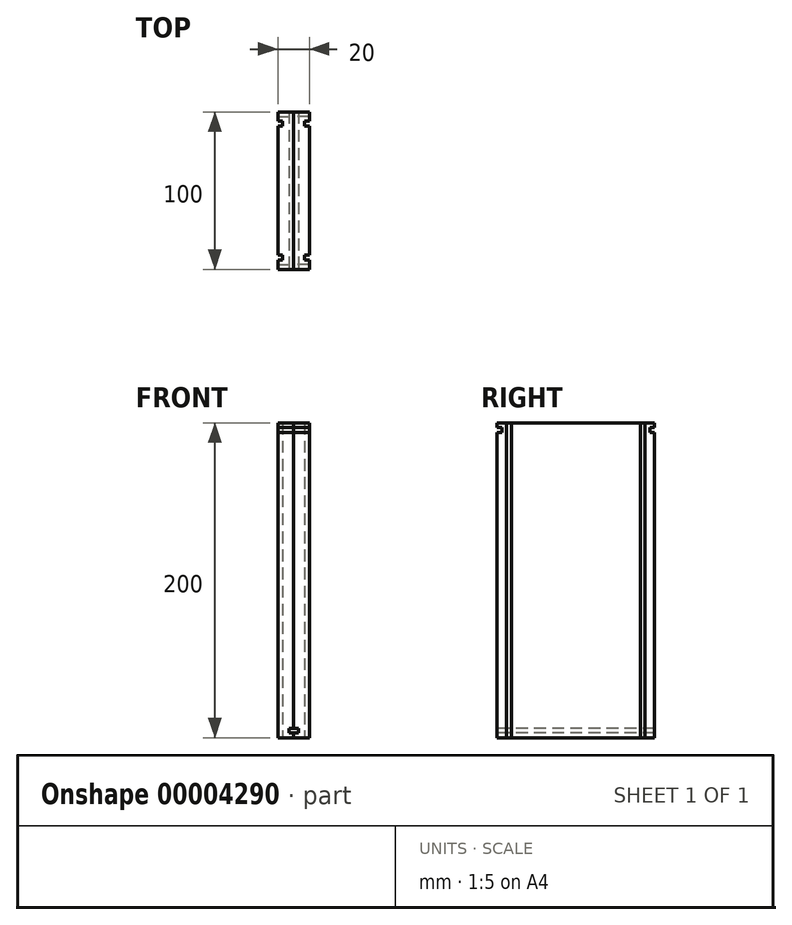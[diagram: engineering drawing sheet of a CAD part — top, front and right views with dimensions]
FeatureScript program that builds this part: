
annotation { "Feature Type Name" : "Feature", "Feature Type Description" : "" }
export const myFeature = defineFeature(function(context is Context, id is Id, definition is map)
    precondition{}
    {
        {
            var Q0;
            Q0=qCreatedBy(makeId("Right.planeOp"),FACE);
            var sketch = newSketch(context, id + "F0", { "sketchPlane" : qUnion([Q0])});
            skLineSegment(sketch, "E0", {"start": v(-61.66, 167.02) * mm, "end": v(38.34, 167.02) * mm});
            skLineSegment(sketch, "E1", {"start": v(38.34, 167.02) * mm, "end": v(38.34, -32.98) * mm});
            skLineSegment(sketch, "E2", {"start": v(38.34, -32.98) * mm, "end": v(-61.66, -32.98) * mm});
            skLineSegment(sketch, "E3", {"start": v(-61.66, -32.98) * mm, "end": v(-61.66, 167.02) * mm});
            skSolve(sketch);
        }
        {
            var Q0;
            Q0=makeQuery(id+"F0.imprint","IMPRINT",FACE,{"disambiguationData":[TD([[makeQuery(id+"F0.imprint","IMPRINT",EDGE,{"derivedFrom":sQuery(id+"F0.wireOp",EDGE,"E0")}),-1.0]])]});
            extrude(context, id + "F1", {"entities" : qUnion([Q0]), "depth" : 10 * mm});
        }
        {
            var Q0;
            Q0=makeQuery(id+"F1.opExtrude","CAP_FACE",FACE,{"disambiguationData":[OSD([sQuery(id+"F0.wireOp",EDGE,"E0"),sQuery(id+"F0.wireOp",EDGE,"E1"),sQuery(id+"F0.wireOp",EDGE,"E2"),sQuery(id+"F0.wireOp",EDGE,"E3")])],"isStart":true});
            var sketch = newSketch(context, id + "F2", { "sketchPlane" : qUnion([Q0])});
            skLineSegment(sketch, "E4.0", {"start": v(-38.34, -29.98) * mm, "end": v(61.66, -29.98) * mm});
            skLineSegment(sketch, "E5.0", {"start": v(-38.34, -26.98) * mm, "end": v(61.66, -26.98) * mm});
            skSolve(sketch);
        }
        {
            var Q0;
            {var subQ2=sQuery(id+"F2.wireOp",EDGE,"E4.0");Q0=makeQuery(id+"F2.imprint","IMPRINT",FACE,{"disambiguationData":[TD([[makeQuery(id+"F2.imprint","IMPRINT",EDGE,{"derivedFrom":subQ2}),1.0]])]});}
            extrude(context, id + "F3", {"entities" : qUnion([Q0]), "operationType" : NewBodyOperationType.REMOVE, "oppositeDirection" : true, "depth" : 3 * mm});
        }
        {
            var Q0;
            Q0=makeQuery(id+"F1.opExtrude","SWEPT_FACE",FACE,{"disambiguationData":[OSD([sQuery(id+"F0.wireOp",EDGE,"E1")])]});
            var sketch = newSketch(context, id + "F4", { "sketchPlane" : qUnion([Q0])});
            skLineSegment(sketch, "E6.0", {"start": v(-10, 164.02) * mm, "end": v(0, 164.02) * mm});
            skLineSegment(sketch, "E7.0", {"start": v(-10, 161.02) * mm, "end": v(0, 161.02) * mm});
            skSolve(sketch);
        }
        {
            var Q0;
            {var subQ4=sQuery(id+"F4.wireOp",EDGE,"E6.0");Q0=makeQuery(id+"F4.imprint","IMPRINT",FACE,{"disambiguationData":[TD([[makeQuery(id+"F4.imprint","IMPRINT",EDGE,{"derivedFrom":subQ4}),-1.0]])]});}
            extrude(context, id + "F5", {"entities" : qUnion([Q0]), "operationType" : NewBodyOperationType.REMOVE, "oppositeDirection" : true, "depth" : 3 * mm});
        }
        {
            var Q0;
            Q0=makeQuery(id+"F1.opExtrude","SWEPT_FACE",FACE,{"disambiguationData":[OSD([sQuery(id+"F0.wireOp",EDGE,"E3")])]});
            var sketch = newSketch(context, id + "F6", { "sketchPlane" : qUnion([Q0])});
            skLineSegment(sketch, "E8.0", {"start": v(10, 164.02) * mm, "end": v(0, 164.02) * mm});
            skLineSegment(sketch, "E9.0", {"start": v(10, 161.02) * mm, "end": v(0, 161.02) * mm});
            skSolve(sketch);
        }
        {
            var Q0;
            {var subQ4=sQuery(id+"F6.wireOp",EDGE,"E8.0");Q0=makeQuery(id+"F6.imprint","IMPRINT",FACE,{"disambiguationData":[TD([[makeQuery(id+"F6.imprint","IMPRINT",EDGE,{"derivedFrom":subQ4}),1.0]])]});}
            extrude(context, id + "F7", {"entities" : qUnion([Q0]), "operationType" : NewBodyOperationType.REMOVE, "oppositeDirection" : true, "depth" : 3 * mm});
        }
        {
            var Q0;
            Q0=makeQuery(id+"F1.opExtrude","CAP_FACE",FACE,{"disambiguationData":[OSD([sQuery(id+"F0.wireOp",EDGE,"E0"),sQuery(id+"F0.wireOp",EDGE,"E1"),sQuery(id+"F0.wireOp",EDGE,"E2"),sQuery(id+"F0.wireOp",EDGE,"E3")])],"isStart":false});
            var sketch = newSketch(context, id + "F8", { "sketchPlane" : qUnion([Q0])});
            skLineSegment(sketch, "E10.0", {"start": v(-55.66, -32.98) * mm, "end": v(-55.66, 161.02) * mm});
            skLineSegment(sketch, "E11.0", {"start": v(32.34, 161.02) * mm, "end": v(32.34, -32.98) * mm});
            skLineSegment(sketch, "E12", {"start": v(-55.66, 161.02) * mm, "end": v(-55.66, 167.02) * mm});
            skLineSegment(sketch, "E13", {"start": v(32.34, 161.02) * mm, "end": v(32.34, 167.02) * mm});
            skLineSegment(sketch, "E14.0", {"start": v(-52.66, -32.98) * mm, "end": v(-52.66, 161.02) * mm});
            skLineSegment(sketch, "E15.0", {"start": v(29.34, 161.02) * mm, "end": v(29.34, -32.98) * mm});
            skLineSegment(sketch, "E16", {"start": v(-52.66, 161.02) * mm, "end": v(-52.66, 167.02) * mm});
            skLineSegment(sketch, "E17", {"start": v(29.34, 161.02) * mm, "end": v(29.34, 167.02) * mm});
            skSolve(sketch);
        }
        {
            var Q0;
            {var subQ2=sQuery(id+"F8.wireOp",EDGE,"E10.0");Q0=makeQuery(id+"F8.imprint","IMPRINT",FACE,{"disambiguationData":[TD([[makeQuery(id+"F8.imprint","IMPRINT",EDGE,{"derivedFrom":subQ2}),-1.0]])]});}
            var Q1;
            {var subQ2=sQuery(id+"F8.wireOp",EDGE,"E11.0");Q1=makeQuery(id+"F8.imprint","IMPRINT",FACE,{"disambiguationData":[TD([[makeQuery(id+"F8.imprint","IMPRINT",EDGE,{"derivedFrom":subQ2}),-1.0]])]});}
            extrude(context, id + "F9", {"entities" : qUnion([Q0, Q1]), "operationType" : NewBodyOperationType.REMOVE, "oppositeDirection" : true, "depth" : 3 * mm});
        }
        {
            var Q0;
            Q0=makeQuery(id+"F1.opExtrude","SWEPT_BODY",BODY,{"disambiguationData":[OSD([sQuery(id+"F0.wireOp",EDGE,"E0"),sQuery(id+"F0.wireOp",EDGE,"E1"),sQuery(id+"F0.wireOp",EDGE,"E2"),sQuery(id+"F0.wireOp",EDGE,"E3")])]});
            var Q1;
            Q1=qCreatedBy(makeId("Right.planeOp"),FACE);
            mirror(context, id + "F10", {"entities" : qUnion([Q0]), "mirrorPlane" : qUnion([Q1])});
        }
    });
